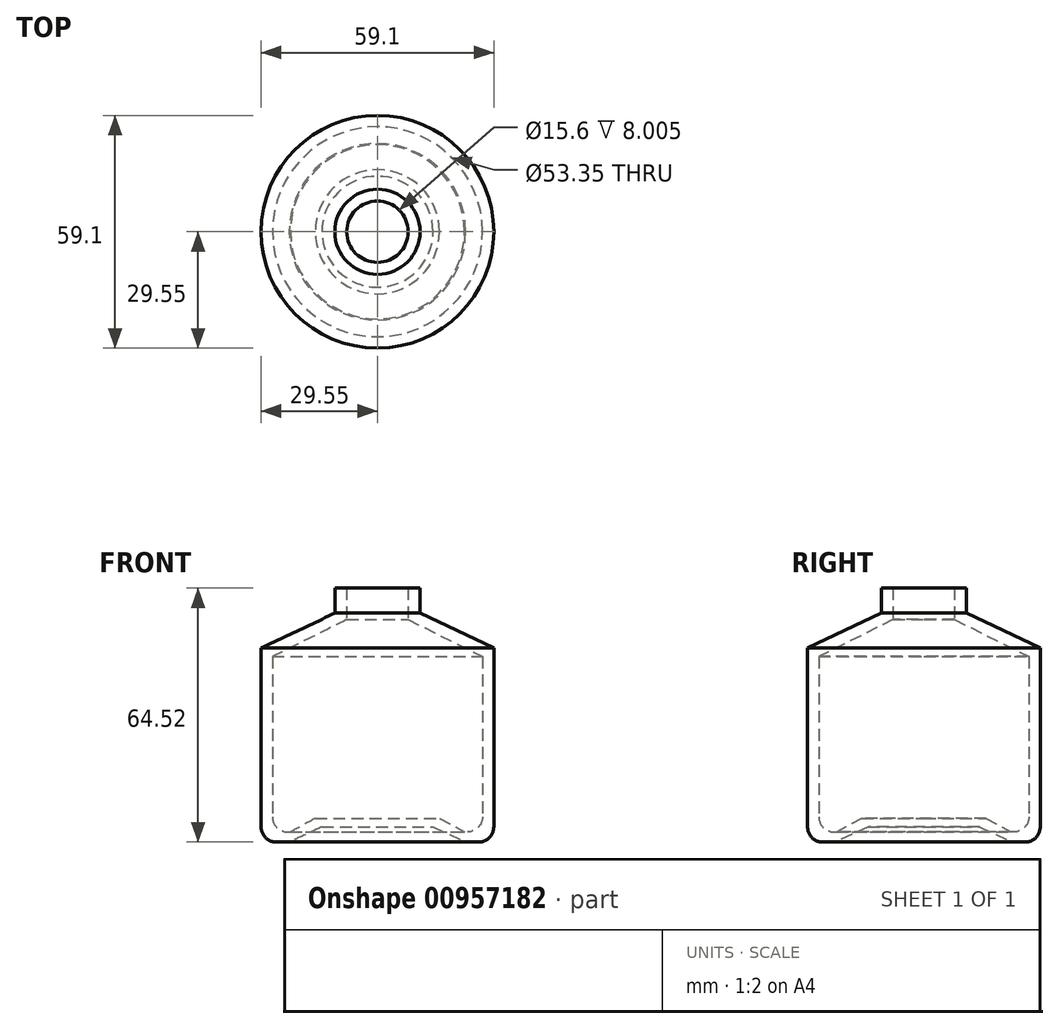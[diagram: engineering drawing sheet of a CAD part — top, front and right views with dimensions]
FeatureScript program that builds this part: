
annotation { "Feature Type Name" : "Feature", "Feature Type Description" : "" }
export const myFeature = defineFeature(function(context is Context, id is Id, definition is map)
    precondition{}
    {
        {
            var Q0;
            Q0=qCreatedBy(makeId("Front.planeOp"),FACE);
            var sketch = newSketch(context, id + "F0", { "sketchPlane" : qUnion([Q0])});
            skLineSegment(sketch, "E0", {"start": v(0, 0) * mm, "end": v(0, 61.34) * mm, "construction": true});
            skLineSegment(sketch, "E1", {"start": v(0, 0) * mm, "end": v(14.11, 0) * mm});
            skLineSegment(sketch, "E2", {"start": v(14.11, 0) * mm, "end": v(22.42, -3.84) * mm});
            skLineSegment(sketch, "E3", {"start": v(22.42, -3.84) * mm, "end": v(25.74, -3.84) * mm});
            skLineSegment(sketch, "E4", {"start": v(29.55, -0.03) * mm, "end": v(29.55, 45.43) * mm});
            skLineSegment(sketch, "E5", {"start": v(29.55, 45.43) * mm, "end": v(10.82, 54.34) * mm});
            skLineSegment(sketch, "E6", {"start": v(10.82, 54.34) * mm, "end": v(10.82, 60.68) * mm});
            skLineSegment(sketch, "E7", {"start": v(10.82, 60.68) * mm, "end": v(7.8, 60.68) * mm});
            skLineSegment(sketch, "E8", {"start": v(7.8, 60.68) * mm, "end": v(7.8, 52.68) * mm});
            skLineSegment(sketch, "E9", {"start": v(7.8, 52.68) * mm, "end": v(26.68, 43.31) * mm});
            skLineSegment(sketch, "E10", {"start": v(26.68, 43.31) * mm, "end": v(26.68, 2.54) * mm});
            skLineSegment(sketch, "E11", {"start": v(22.87, -1.27) * mm, "end": v(22.12, -1.27) * mm});
            skLineSegment(sketch, "E12", {"start": v(22.12, -1.27) * mm, "end": v(15.78, 2.2) * mm});
            skLineSegment(sketch, "E13", {"start": v(15.78, 2.2) * mm, "end": v(0, 2.2) * mm});
            skLineSegment(sketch, "E14", {"start": v(0, 2.2) * mm, "end": v(0, 0) * mm});
            skPoint(sketch, "E15.visualSharp", {"position": v(29.55, -3.84) * mm});
            skArc(sketch, "E15.filletArc", {"start": v(25.74, -3.84) * mm, "mid": v(28.43, -2.72) * mm, "end": v(29.55, -0.03) * mm});
            skPoint(sketch, "E16.visualSharp", {"position": v(26.68, -1.27) * mm});
            skArc(sketch, "E16.filletArc", {"start": v(22.87, -1.27) * mm, "mid": v(25.56, -0.15) * mm, "end": v(26.68, 2.54) * mm});
            skSolve(sketch);
        }
        {
            var Q0;
            Q0 = qSketchRegion(id + "F0", true);
            var Q1;
            Q1=sQuery(id+"F0.wireOp",EDGE,"E0");
            revolve(context, id + "F1", {"surfaceOperationType" : NewSurfaceOperationType.NEW, "entities" : qUnion([Q0]), "axis" : qUnion([Q1]), "revolveType" : RevolveType.FULL});
        }
    });
